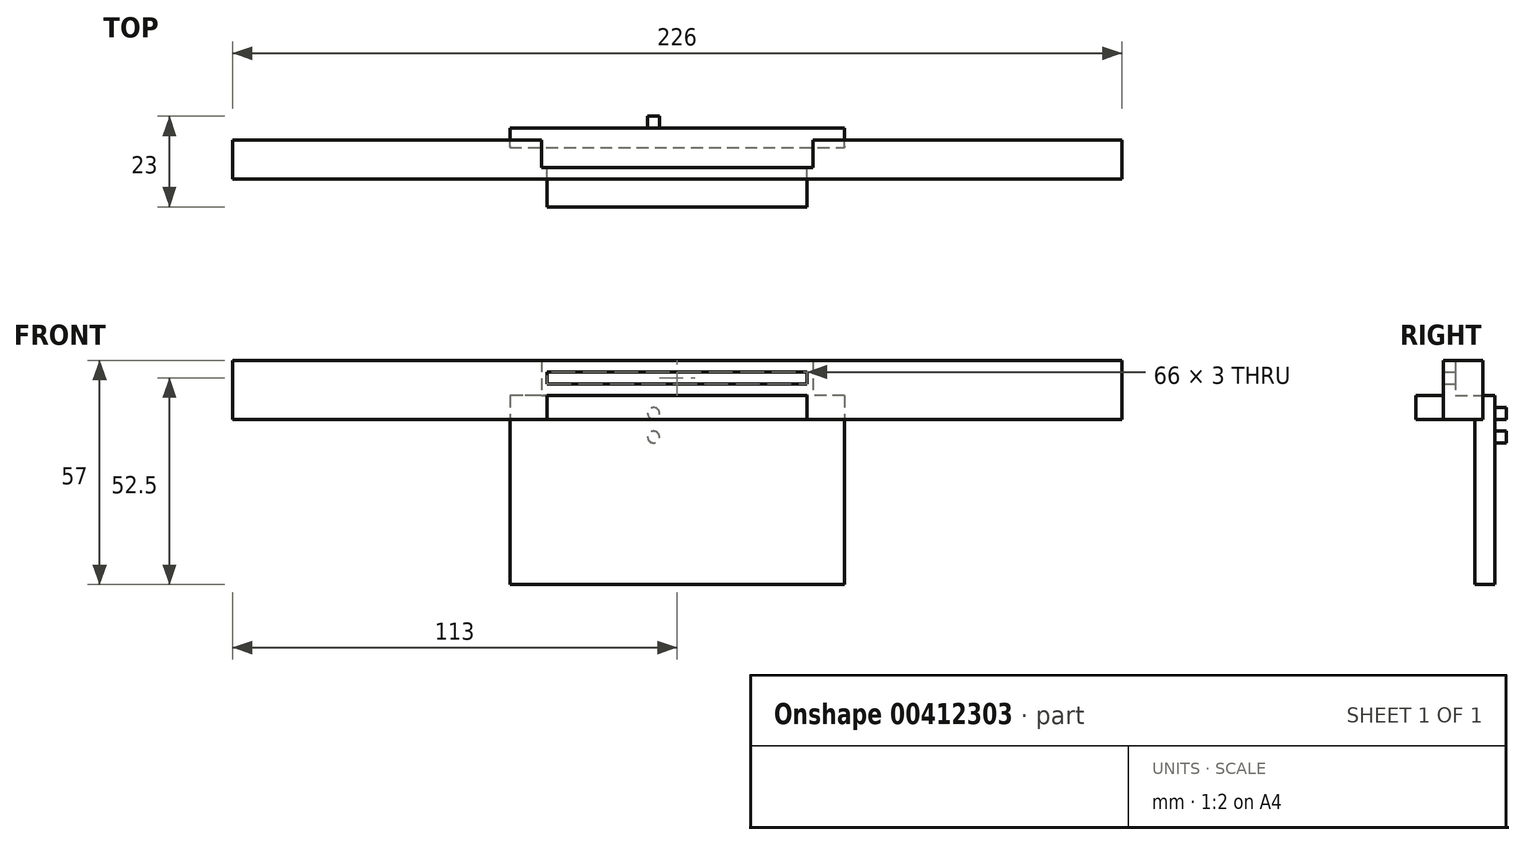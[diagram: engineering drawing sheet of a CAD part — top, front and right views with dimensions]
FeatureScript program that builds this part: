
annotation { "Feature Type Name" : "Feature", "Feature Type Description" : "" }
export const myFeature = defineFeature(function(context is Context, id is Id, definition is map)
    precondition{}
    {
        {
            var Q0;
            Q0=qCreatedBy(makeId("Front.planeOp"),FACE);
            var sketch = newSketch(context, id + "F0", { "sketchPlane" : qUnion([Q0])});
            skLineSegment(sketch, "E0.bottom", {"start": v(113, 7.5) * mm, "end": v(-113, 7.5) * mm});
            skLineSegment(sketch, "E0.top", {"start": v(113, -7.5) * mm, "end": v(-113, -7.5) * mm});
            skLineSegment(sketch, "E0.left", {"start": v(113, 7.5) * mm, "end": v(113, -7.5) * mm});
            skLineSegment(sketch, "E0.right", {"start": v(-113, 7.5) * mm, "end": v(-113, -7.5) * mm});
            skPoint(sketch, "E0.middle", {"position": v(0, 0) * mm});
            skSolve(sketch);
        }
        {
            var Q0;
            Q0 = qSketchRegion(id + "F0", true);
            extrude(context, id + "F1", {"entities" : qUnion([Q0]), "depth" : 10 * mm});
        }
        {
            var Q0;
            Q0=makeQuery(id+"F1.opExtrude","CAP_FACE",FACE,{"disambiguationData":[OSD([sQuery(id+"F0.wireOp",EDGE,"E0.bottom"),sQuery(id+"F0.wireOp",EDGE,"E0.top"),sQuery(id+"F0.wireOp",EDGE,"E0.left"),sQuery(id+"F0.wireOp",EDGE,"E0.right")])],"isStart":false});
            var sketch = newSketch(context, id + "F2", { "sketchPlane" : qUnion([Q0])});
            skLineSegment(sketch, "E1.bottom", {"start": v(-33, -7.5) * mm, "end": v(33, -7.5) * mm});
            skLineSegment(sketch, "E1.top", {"start": v(-33, -1.5) * mm, "end": v(33, -1.5) * mm});
            skLineSegment(sketch, "E1.left", {"start": v(-33, -7.5) * mm, "end": v(-33, -1.5) * mm});
            skLineSegment(sketch, "E1.right", {"start": v(33, -7.5) * mm, "end": v(33, -1.5) * mm});
            skSolve(sketch);
        }
        {
            var Q0;
            Q0 = qSketchRegion(id + "F2", true);
            extrude(context, id + "F3", {"entities" : qUnion([Q0]), "operationType" : NewBodyOperationType.ADD, "depth" : 7 * mm});
        }
        {
            var Q0;
            Q0=makeQuery(id+"F1.opExtrude","CAP_FACE",FACE,{"disambiguationData":[OSD([sQuery(id+"F0.wireOp",EDGE,"E0.bottom"),sQuery(id+"F0.wireOp",EDGE,"E0.top"),sQuery(id+"F0.wireOp",EDGE,"E0.left"),sQuery(id+"F0.wireOp",EDGE,"E0.right")])],"isStart":true});
            var sketch = newSketch(context, id + "F4", { "sketchPlane" : qUnion([Q0])});
            skLineSegment(sketch, "E2.bottom", {"start": v(-42.5, 0) * mm, "end": v(42.5, 0) * mm});
            skLineSegment(sketch, "E2.top", {"start": v(-42.5, -49.5) * mm, "end": v(42.5, -49.5) * mm});
            skLineSegment(sketch, "E2.left", {"start": v(-42.5, 0) * mm, "end": v(-42.5, -49.5) * mm});
            skLineSegment(sketch, "E2.right", {"start": v(42.5, 0) * mm, "end": v(42.5, -49.5) * mm});
            skSolve(sketch);
        }
        {
            var Q0;
            Q0 = qSketchRegion(id + "F4", true);
            extrude(context, id + "F5", {"entities" : qUnion([Q0]), "operationType" : NewBodyOperationType.ADD, "depth" : 3 * mm, "hasSecondDirection" : true, "secondDirectionOppositeDirection" : true, "secondDirectionDepth" : 2 * mm});
        }
        {
            var Q0;
            Q0=makeQuery(id+"F1.opExtrude","CAP_FACE",FACE,{"disambiguationData":[OSD([sQuery(id+"F0.wireOp",EDGE,"E0.bottom"),sQuery(id+"F0.wireOp",EDGE,"E0.top"),sQuery(id+"F0.wireOp",EDGE,"E0.left"),sQuery(id+"F0.wireOp",EDGE,"E0.right")])],"isStart":true});
            var sketch = newSketch(context, id + "F6", { "sketchPlane" : qUnion([Q0])});
            skLineSegment(sketch, "E3.bottom", {"start": v(34.5, 16.5) * mm, "end": v(-34.5, 16.5) * mm});
            skLineSegment(sketch, "E3.top", {"start": v(34.5, -1.5) * mm, "end": v(-34.5, -1.5) * mm});
            skLineSegment(sketch, "E3.left", {"start": v(34.5, 16.5) * mm, "end": v(34.5, -1.5) * mm});
            skLineSegment(sketch, "E3.right", {"start": v(-34.5, 16.5) * mm, "end": v(-34.5, -1.5) * mm});
            skPoint(sketch, "E3.middle", {"position": v(0, 7.5) * mm});
            skSolve(sketch);
        }
        {
            var Q0;
            Q0 = qSketchRegion(id + "F6", true);
            extrude(context, id + "F7", {"entities" : qUnion([Q0]), "operationType" : NewBodyOperationType.REMOVE, "oppositeDirection" : true, "depth" : 7 * mm});
        }
        {
            var Q0;
            Q0=makeQuery(id+"F7.boolean.opBoolean","COPY",FACE,{"derivedFrom":makeQuery(id+"F7.opExtrude","CAP_FACE",FACE,{"disambiguationData":[OSD([sQuery(id+"F6.wireOp",EDGE,"E3.bottom"),sQuery(id+"F6.wireOp",EDGE,"E3.top"),sQuery(id+"F6.wireOp",EDGE,"E3.left"),sQuery(id+"F6.wireOp",EDGE,"E3.right")])],"isStart":false})});
            var sketch = newSketch(context, id + "F8", { "sketchPlane" : qUnion([Q0])});
            skLineSegment(sketch, "E4.bottom", {"start": v(33, 4.5) * mm, "end": v(-33, 4.5) * mm});
            skLineSegment(sketch, "E4.top", {"start": v(33, 1.5) * mm, "end": v(-33, 1.5) * mm});
            skLineSegment(sketch, "E4.left", {"start": v(33, 4.5) * mm, "end": v(33, 1.5) * mm});
            skLineSegment(sketch, "E4.right", {"start": v(-33, 4.5) * mm, "end": v(-33, 1.5) * mm});
            skPoint(sketch, "E4.middle", {"position": v(0, 3) * mm});
            skSolve(sketch);
        }
        {
            var Q0;
            Q0 = qSketchRegion(id + "F8", true);
            extrude(context, id + "F9", {"entities" : qUnion([Q0]), "operationType" : NewBodyOperationType.REMOVE, "oppositeDirection" : true, "depth" : 25 * mm});
        }
        {
            var Q0;
            Q0=makeQuery(id+"F5.opExtrude","CAP_FACE",FACE,{"disambiguationData":[OSD([sQuery(id+"F4.wireOp",EDGE,"E2.bottom"),sQuery(id+"F4.wireOp",EDGE,"E2.top"),sQuery(id+"F4.wireOp",EDGE,"E2.left"),sQuery(id+"F4.wireOp",EDGE,"E2.right")])],"isStart":false});
            var sketch = newSketch(context, id + "F10", { "sketchPlane" : qUnion([Q0])});
            skLineSegment(sketch, "E5.bottom", {"start": v(-42.5, 0) * mm, "end": v(42.5, 0) * mm});
            skLineSegment(sketch, "E5.top", {"start": v(-42.5, -1) * mm, "end": v(42.5, -1) * mm});
            skLineSegment(sketch, "E5.left", {"start": v(-42.5, 0) * mm, "end": v(-42.5, -1) * mm});
            skLineSegment(sketch, "E5.right", {"start": v(42.5, 0) * mm, "end": v(42.5, -1) * mm});
            skSolve(sketch);
        }
        {
            var Q0;
            Q0 = qSketchRegion(id + "F10", true);
            extrude(context, id + "F11", {"entities" : qUnion([Q0]), "operationType" : NewBodyOperationType.REMOVE, "oppositeDirection" : true, "depth" : 3 * mm});
        }
        {
            var Q0;
            Q0=makeQuery(id+"F5.opExtrude","CAP_FACE",FACE,{"disambiguationData":[OSD([sQuery(id+"F4.wireOp",EDGE,"E2.bottom"),sQuery(id+"F4.wireOp",EDGE,"E2.top"),sQuery(id+"F4.wireOp",EDGE,"E2.left"),sQuery(id+"F4.wireOp",EDGE,"E2.right")])],"isStart":false});
            var sketch = newSketch(context, id + "F12", { "sketchPlane" : qUnion([Q0])});
            skLineSegment(sketch, "E6.bottom", {"start": v(-42.5, -1) * mm, "end": v(42.5, -1) * mm});
            skLineSegment(sketch, "E6.top", {"start": v(-42.5, -1.5) * mm, "end": v(42.5, -1.5) * mm});
            skLineSegment(sketch, "E6.left", {"start": v(-42.5, -1) * mm, "end": v(-42.5, -1.5) * mm});
            skLineSegment(sketch, "E6.right", {"start": v(42.5, -1) * mm, "end": v(42.5, -1.5) * mm});
            skSolve(sketch);
        }
        {
            var Q0;
            Q0 = qSketchRegion(id + "F12", true);
            extrude(context, id + "F13", {"entities" : qUnion([Q0]), "operationType" : NewBodyOperationType.REMOVE, "oppositeDirection" : true, "depth" : 3 * mm});
        }
        {
            var Q0;
            Q0=makeQuery(id+"F5.opExtrude","CAP_FACE",FACE,{"disambiguationData":[OSD([sQuery(id+"F4.wireOp",EDGE,"E2.bottom"),sQuery(id+"F4.wireOp",EDGE,"E2.top"),sQuery(id+"F4.wireOp",EDGE,"E2.left"),sQuery(id+"F4.wireOp",EDGE,"E2.right")])],"isStart":false});
            var sketch = newSketch(context, id + "F14", { "sketchPlane" : qUnion([Q0])});
            skCircle(sketch, "E7", {"center": v(6, -6) * mm, "radius": 1.5 * mm});
            skCircle(sketch, "E8", {"center": v(6, -12) * mm, "radius": 1.5 * mm});
            skSolve(sketch);
        }
        {
            var Q0;
            Q0 = qSketchRegion(id + "F14", true);
            extrude(context, id + "F15", {"entities" : qUnion([Q0]), "operationType" : NewBodyOperationType.ADD, "depth" : 3 * mm});
        }
    });
